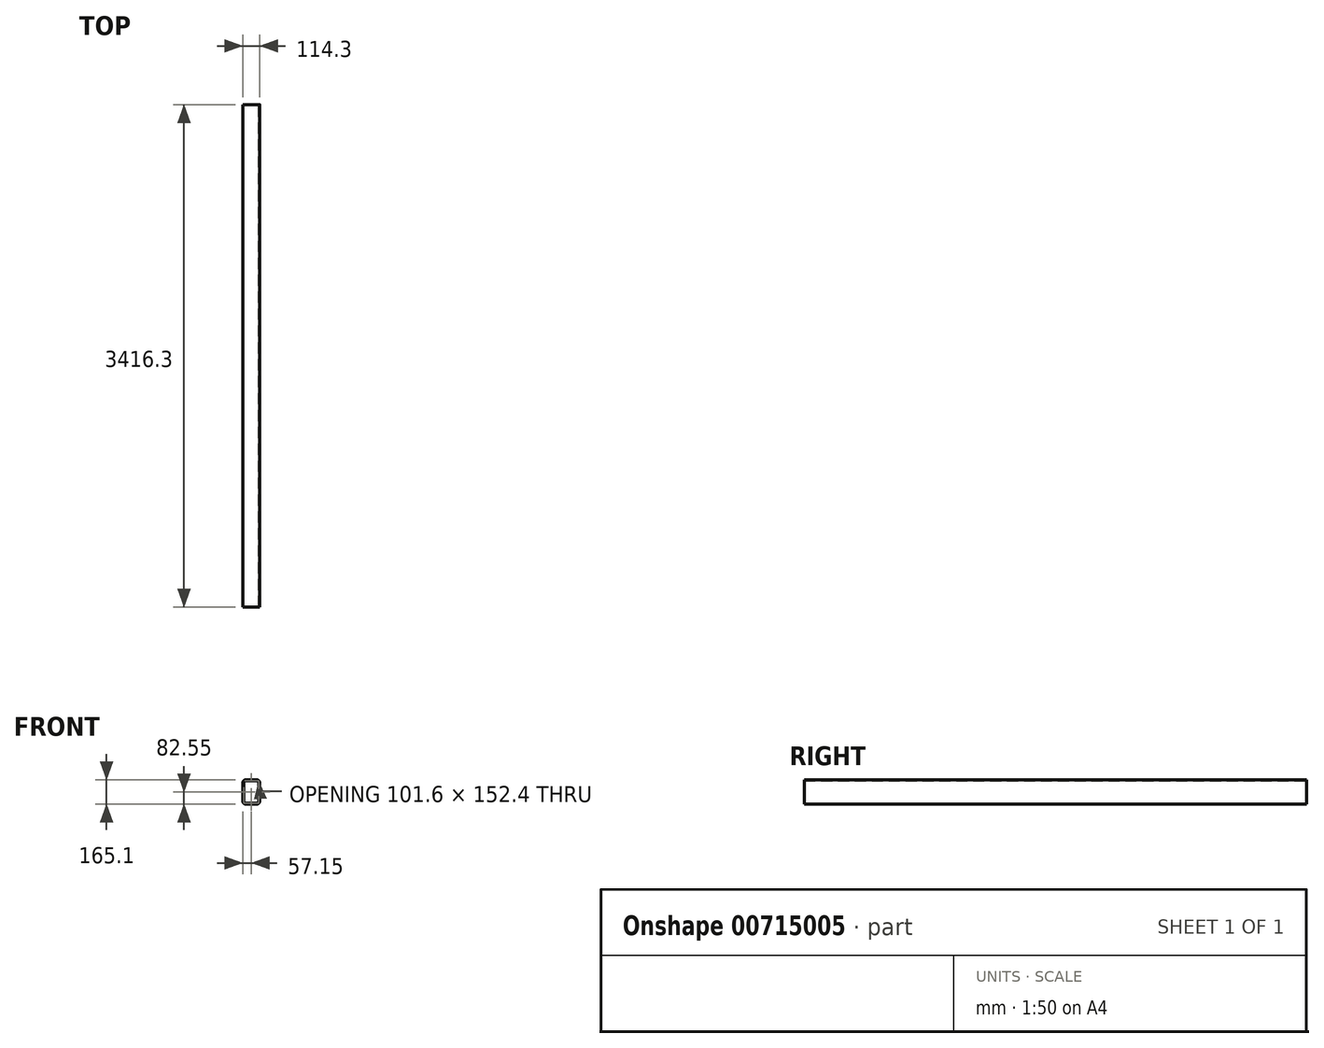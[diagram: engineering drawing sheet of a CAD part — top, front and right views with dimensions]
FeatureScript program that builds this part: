
annotation { "Feature Type Name" : "Feature", "Feature Type Description" : "" }
export const myFeature = defineFeature(function(context is Context, id is Id, definition is map)
    precondition{}
    {
        {
            var Q0;
            Q0=qCreatedBy(makeId("Front.planeOp"),FACE);
            var sketch = newSketch(context, id + "F0", { "sketchPlane" : qUnion([Q0])});
            skLineSegment(sketch, "E0.bottom", {"start": v(38.1, -76.2) * mm, "end": v(-38.1, -76.2) * mm});
            skLineSegment(sketch, "E0.top", {"start": v(38.1, 76.2) * mm, "end": v(-38.1, 76.2) * mm});
            skLineSegment(sketch, "E0.left", {"start": v(50.8, -63.5) * mm, "end": v(50.8, 63.5) * mm});
            skLineSegment(sketch, "E0.right", {"start": v(-50.8, -63.5) * mm, "end": v(-50.8, 63.5) * mm});
            skPoint(sketch, "E0.middle", {"position": v(0, 0) * mm});
            skPoint(sketch, "E1.visualSharp", {"position": v(-50.8, 76.2) * mm});
            skArc(sketch, "E1.filletArc", {"start": v(-38.1, 76.2) * mm, "mid": v(-47.08, 72.48) * mm, "end": v(-50.8, 63.5) * mm});
            skPoint(sketch, "E2.visualSharp", {"position": v(50.8, 76.2) * mm});
            skArc(sketch, "E2.filletArc", {"start": v(50.8, 63.5) * mm, "mid": v(47.08, 72.48) * mm, "end": v(38.1, 76.2) * mm});
            skPoint(sketch, "E3.visualSharp", {"position": v(50.8, -76.2) * mm});
            skArc(sketch, "E3.filletArc", {"start": v(38.1, -76.2) * mm, "mid": v(47.08, -72.48) * mm, "end": v(50.8, -63.5) * mm});
            skPoint(sketch, "E4.visualSharp", {"position": v(-50.8, -76.2) * mm});
            skArc(sketch, "E4.filletArc", {"start": v(-50.8, -63.5) * mm, "mid": v(-47.08, -72.48) * mm, "end": v(-38.1, -76.2) * mm});
            skLineSegment(sketch, "E5.0", {"start": v(57.15, -63.5) * mm, "end": v(57.15, 63.5) * mm});
            skArc(sketch, "E5.1", {"start": v(38.1, -82.55) * mm, "mid": v(51.57, -76.97) * mm, "end": v(57.15, -63.5) * mm});
            skArc(sketch, "E5.2", {"start": v(57.15, 63.5) * mm, "mid": v(51.57, 76.97) * mm, "end": v(38.1, 82.55) * mm});
            skLineSegment(sketch, "E5.3", {"start": v(38.1, -82.55) * mm, "end": v(-38.1, -82.55) * mm});
            skLineSegment(sketch, "E5.4", {"start": v(38.1, 82.55) * mm, "end": v(-38.1, 82.55) * mm});
            skArc(sketch, "E5.5", {"start": v(-38.1, 82.55) * mm, "mid": v(-51.57, 76.97) * mm, "end": v(-57.15, 63.5) * mm});
            skLineSegment(sketch, "E5.6", {"start": v(-57.15, -63.5) * mm, "end": v(-57.15, 63.5) * mm});
            skArc(sketch, "E5.7", {"start": v(-57.15, -63.5) * mm, "mid": v(-51.57, -76.97) * mm, "end": v(-38.1, -82.55) * mm});
            skSolve(sketch);
        }
        {
            var Q0;
            Q0=makeQuery(id+"F0.imprint","IMPRINT",FACE,{"disambiguationData":[TD([[makeQuery(id+"F0.imprint","IMPRINT",EDGE,{"derivedFrom":sQuery(id+"F0.wireOp",EDGE,"E0.bottom")}),1.0]])]});
            extrude(context, id + "F1", {"entities" : qUnion([Q0]), "depth" : 3416.3 * mm, "offsetDistance" : 25.4 * mm});
        }
    });
